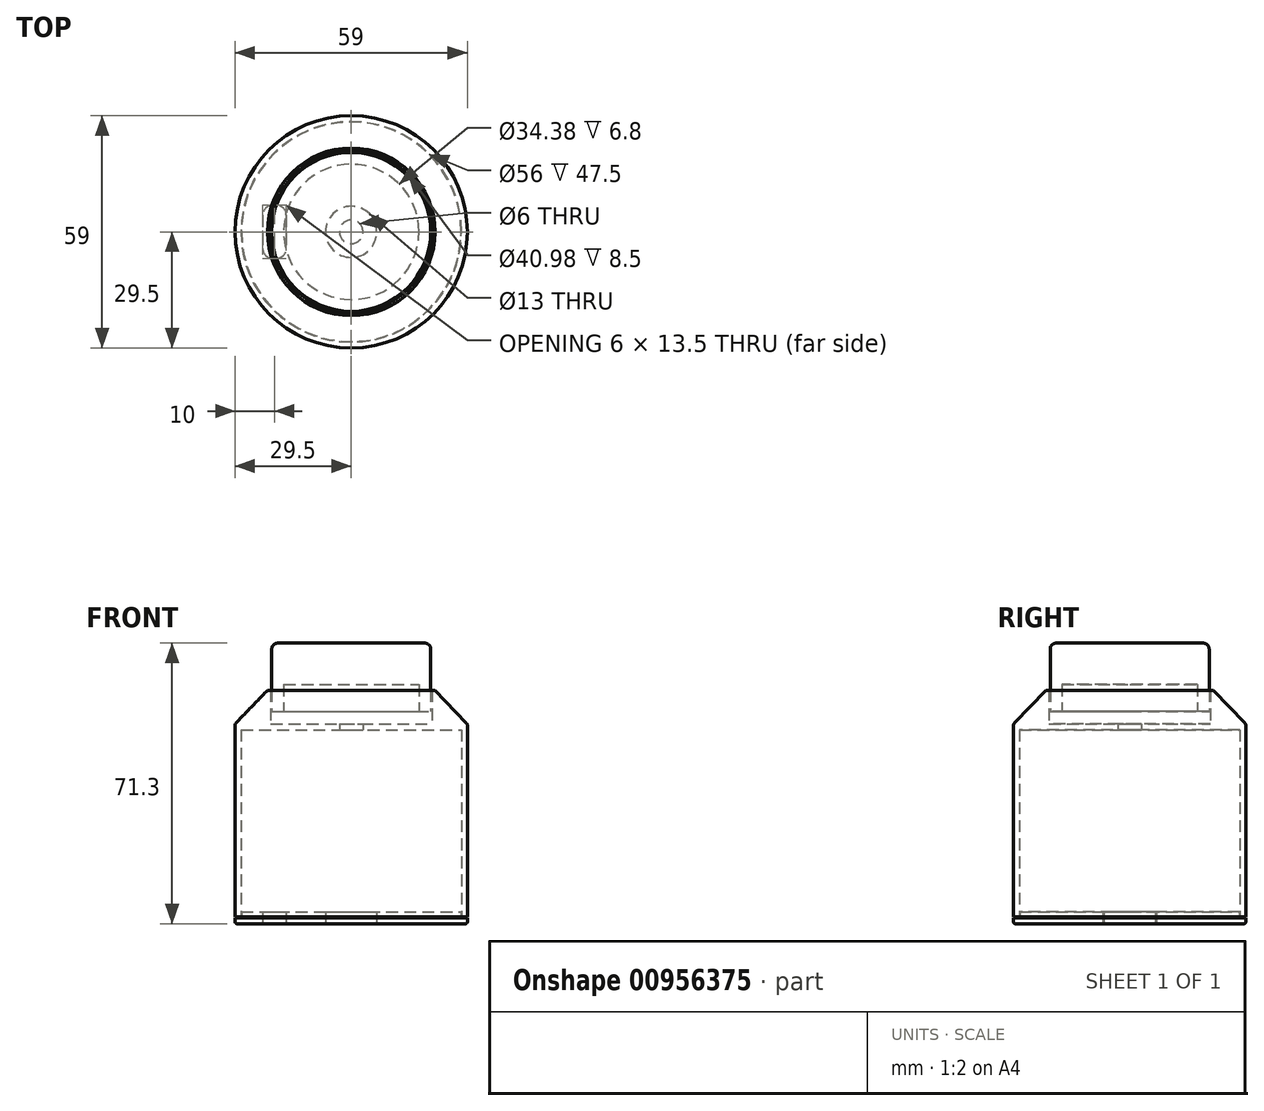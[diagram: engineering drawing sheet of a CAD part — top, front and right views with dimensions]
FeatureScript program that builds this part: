
annotation { "Feature Type Name" : "Feature", "Feature Type Description" : "" }
export const myFeature = defineFeature(function(context is Context, id is Id, definition is map)
    precondition{}
    {
        {
            var Q0;
            Q0=qCreatedBy(makeId("Top.planeOp"),FACE);
            var sketch = newSketch(context, id + "F0", { "sketchPlane" : qUnion([Q0])});
            skCircle(sketch, "E0", {"center": v(0, 0) * mm, "radius": 29.5 * mm});
            skSolve(sketch);
        }
        {
            var Q0;
            Q0=qCreatedBy(makeId("Front.planeOp"),FACE);
            var sketch = newSketch(context, id + "F1", { "sketchPlane" : qUnion([Q0])});
            skLineSegment(sketch, "E1", {"start": v(-29.5, 0) * mm, "end": v(-29.5, 49) * mm});
            skLineSegment(sketch, "E2.1", {"start": v(-29.5, 0) * mm, "end": v(29.5, 0) * mm, "construction": true});
            skLineSegment(sketch, "E3", {"start": v(-29.5, 49) * mm, "end": v(-21.3, 57.5) * mm});
            skLineSegment(sketch, "E4", {"start": v(-21.3, 57.5) * mm, "end": v(-20.5, 57.5) * mm});
            skLineSegment(sketch, "E5", {"start": v(-20.5, 57.5) * mm, "end": v(-20.5, 47.5) * mm, "construction": true});
            skLineSegment(sketch, "E6", {"start": v(-20.5, 47.5) * mm, "end": v(-28, 47.5) * mm});
            skLineSegment(sketch, "E7", {"start": v(-28, 47.5) * mm, "end": v(-28, 0) * mm});
            skLineSegment(sketch, "E8", {"start": v(-28, 0) * mm, "end": v(-29.5, 0) * mm});
            skLineSegment(sketch, "E9", {"start": v(-20.5, 57.5) * mm, "end": v(-20.5, 49) * mm});
            skLineSegment(sketch, "E10", {"start": v(-20.5, 49) * mm, "end": v(-3, 49) * mm});
            skLineSegment(sketch, "E11", {"start": v(-3, 49) * mm, "end": v(-3, 47.5) * mm});
            skLineSegment(sketch, "E12", {"start": v(-3, 47.5) * mm, "end": v(-20.5, 47.5) * mm});
            skLineSegment(sketch, "E13", {"start": v(0, 0) * mm, "end": v(0, 67.8) * mm, "construction": true});
            skSolve(sketch);
        }
        {
            var Q0;
            Q0 = qSketchRegion(id + "F1", true);
            var Q1;
            Q1=sQuery(id+"F1.wireOp",EDGE,"E13");
            revolve(context, id + "F2", {"surfaceOperationType" : NewSurfaceOperationType.NEW, "entities" : qUnion([Q0]), "axis" : qUnion([Q1]), "revolveType" : RevolveType.FULL});
        }
        {
            var Q0;
            Q0=qCreatedBy(makeId("Front.planeOp"),FACE);
            var sketch = newSketch(context, id + "F3", { "sketchPlane" : qUnion([Q0])});
            skLineSegment(sketch, "E14", {"start": v(-20.2, 52.2) * mm, "end": v(-20.2, 69.5) * mm});
            skLineSegment(sketch, "E15", {"start": v(-20.2, 69.5) * mm, "end": v(0, 69.5) * mm});
            skLineSegment(sketch, "E16", {"start": v(0, 69.5) * mm, "end": v(0, 59) * mm});
            skLineSegment(sketch, "E17", {"start": v(0, 59) * mm, "end": v(-17.2, 59) * mm});
            skLineSegment(sketch, "E18", {"start": v(-17.2, 59) * mm, "end": v(-17.2, 52.2) * mm});
            skLineSegment(sketch, "E19", {"start": v(-17.2, 52.2) * mm, "end": v(-20.2, 52.2) * mm});
            skSolve(sketch);
        }
        {
            var Q0;
            Q0=makeQuery(id+"F3.imprint","IMPRINT",FACE,{"disambiguationData":[TD([[makeQuery(id+"F3.imprint","IMPRINT",EDGE,{"derivedFrom":sQuery(id+"F3.wireOp",EDGE,"E14")}),-1.0]])]});
            var Q1;
            Q1=sQuery(id+"F1.wireOp",EDGE,"E13");
            revolve(context, id + "F4", {"surfaceOperationType" : NewSurfaceOperationType.NEW, "entities" : qUnion([Q0]), "axis" : qUnion([Q1]), "revolveType" : RevolveType.FULL});
        }
        {
            var Q0;
            Q0=makeQuery(id+"F4.opRevolve","SWEPT_EDGE",EDGE,{"disambiguationData":[OSD([sQuery(id+"F3.wireOp",EDGE,"E14"),sQuery(id+"F3.wireOp",EDGE,"E15")])]});
            fillet(context, id + "F5", {"entities" : qUnion([Q0]), "radius" : 1.5 * mm, "tangentPropagation" : true, "allowEdgeOverflow" : false});
        }
        {
            var Q0;
            Q0=makeQuery(id+"F2.opRevolve","SWEPT_EDGE",EDGE,{"disambiguationData":[OSD([sQuery(id+"F1.wireOp",EDGE,"E1"),sQuery(id+"F1.wireOp",EDGE,"E3")])]});
            fillet(context, id + "F6", {"entities" : qUnion([Q0]), "radius" : 1 * mm, "tangentPropagation" : true, "allowEdgeOverflow" : false});
        }
        {
            var Q0;
            Q0=qCreatedBy(makeId("Front.planeOp"),FACE);
            var sketch = newSketch(context, id + "F7", { "sketchPlane" : qUnion([Q0])});
            skLineSegment(sketch, "E20", {"start": v(0, -1.8) * mm, "end": v(-29.5, -1.8) * mm, "construction": true});
            skLineSegment(sketch, "E21", {"start": v(-29.5, -1.8) * mm, "end": v(-29.5, -0.3) * mm});
            skLineSegment(sketch, "E22", {"start": v(-29.5, -0.3) * mm, "end": v(-27.9, -0.3) * mm});
            skLineSegment(sketch, "E23", {"start": v(-27.9, -0.3) * mm, "end": v(-27.9, 1.2) * mm});
            skLineSegment(sketch, "E24", {"start": v(-27.9, 1.2) * mm, "end": v(0, 1.2) * mm, "construction": true});
            skLineSegment(sketch, "E25", {"start": v(0, 1.2) * mm, "end": v(0, -1.8) * mm, "construction": true});
            skLineSegment(sketch, "E26", {"start": v(-29.5, -1.8) * mm, "end": v(-6.5, -1.8) * mm});
            skLineSegment(sketch, "E27", {"start": v(-6.5, -1.8) * mm, "end": v(-6.5, 1.2) * mm});
            skLineSegment(sketch, "E28", {"start": v(-6.5, 1.2) * mm, "end": v(-27.9, 1.2) * mm});
            skSolve(sketch);
        }
        {
            var Q0;
            Q0=makeQuery(id+"F7.imprint","IMPRINT",FACE,{"disambiguationData":[TD([[makeQuery(id+"F7.imprint","IMPRINT",EDGE,{"derivedFrom":sQuery(id+"F7.wireOp",EDGE,"E21")}),-1.0]])]});
            var Q1;
            Q1=sQuery(id+"F1.wireOp",EDGE,"E13");
            revolve(context, id + "F8", {"surfaceOperationType" : NewSurfaceOperationType.NEW, "entities" : qUnion([Q0]), "axis" : qUnion([Q1]), "revolveType" : RevolveType.FULL});
        }
        {
            var Q0;
            Q0=makeQuery(id+"F8.opRevolve","SWEPT_FACE",FACE,{"disambiguationData":[OSD([sQuery(id+"F7.wireOp",EDGE,"E26")])]});
            var sketch = newSketch(context, id + "F9", { "sketchPlane" : qUnion([Q0])});
            skLineSegment(sketch, "E29.bottom", {"start": v(-20, -6.75) * mm, "end": v(-19, -6.75) * mm});
            skLineSegment(sketch, "E29.top", {"start": v(-20, 6.75) * mm, "end": v(-19, 6.75) * mm});
            skLineSegment(sketch, "E29.left", {"start": v(-22.5, -4.25) * mm, "end": v(-22.5, 4.25) * mm});
            skLineSegment(sketch, "E29.right", {"start": v(-16.5, -4.25) * mm, "end": v(-16.5, 4.25) * mm});
            skPoint(sketch, "E29.middle", {"position": v(-19.5, 0) * mm});
            skPoint(sketch, "E30.visualSharp", {"position": v(-16.5, -6.75) * mm});
            skArc(sketch, "E30.filletArc", {"start": v(-19, -6.75) * mm, "mid": v(-17.23, -6.02) * mm, "end": v(-16.5, -4.25) * mm});
            skPoint(sketch, "E31.visualSharp", {"position": v(-22.5, -6.75) * mm});
            skArc(sketch, "E31.filletArc", {"start": v(-22.5, -4.25) * mm, "mid": v(-21.77, -6.02) * mm, "end": v(-20, -6.75) * mm});
            skPoint(sketch, "E32.visualSharp", {"position": v(-22.5, 6.75) * mm});
            skArc(sketch, "E32.filletArc", {"start": v(-20, 6.75) * mm, "mid": v(-21.77, 6.02) * mm, "end": v(-22.5, 4.25) * mm});
            skPoint(sketch, "E33.visualSharp", {"position": v(-16.5, 6.75) * mm});
            skArc(sketch, "E33.filletArc", {"start": v(-16.5, 4.25) * mm, "mid": v(-17.23, 6.02) * mm, "end": v(-19, 6.75) * mm});
            skSolve(sketch);
        }
        {
            var Q0;
            Q0 = qSketchRegion(id + "F9", true);
            extrude(context, id + "F10", {"entities" : qUnion([Q0]), "operationType" : NewBodyOperationType.REMOVE, "oppositeDirection" : true, "depth" : 25 * mm, "offsetDistance" : 25 * mm});
        }
        {
            var Q0;
            Q0=makeQuery(id+"F8.opRevolve","SWEPT_EDGE",EDGE,{"disambiguationData":[OSD([sQuery(id+"F7.wireOp",EDGE,"E21"),sQuery(id+"F7.wireOp",EDGE,"E26")])]});
            fillet(context, id + "F11", {"entities" : qUnion([Q0]), "radius" : 0.5 * mm, "tangentPropagation" : true, "allowEdgeOverflow" : false});
        }
    });
